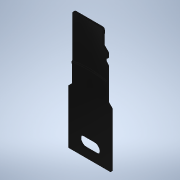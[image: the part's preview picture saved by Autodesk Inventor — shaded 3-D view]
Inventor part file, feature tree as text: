
AUTODESK INVENTOR PART (.ipt)
format: ipt  version: 2022 (Build 260153000, 153)  size: 251,392 bytes
history: native  units: mm
features: extrude x1, sketch x1, fillet x1
ambient origin geometry x8: Origin, YZ Plane, XZ Plane, XY Plane, X Axis, Y Axis, Z Axis, Center Point
bodies: Volumenkörper1 (feature_tree)
feature tree (3):
  extrude  "Extrusion1"  Depth=38.0mm
  sketch  "Skizze1"  dims[d0=90.0deg d1=38.0mm d2=1.2mm d3=1.2mm d4=17.0mm d5=17.0mm d6=4.0mm d7=5.0mm d8=5.0mm d9=3.17mm d10=45.0deg d11=135.0deg d12=0.7mm d13=0.0mm]
  fillet  "Fillet2"  Radius=1.2mm
